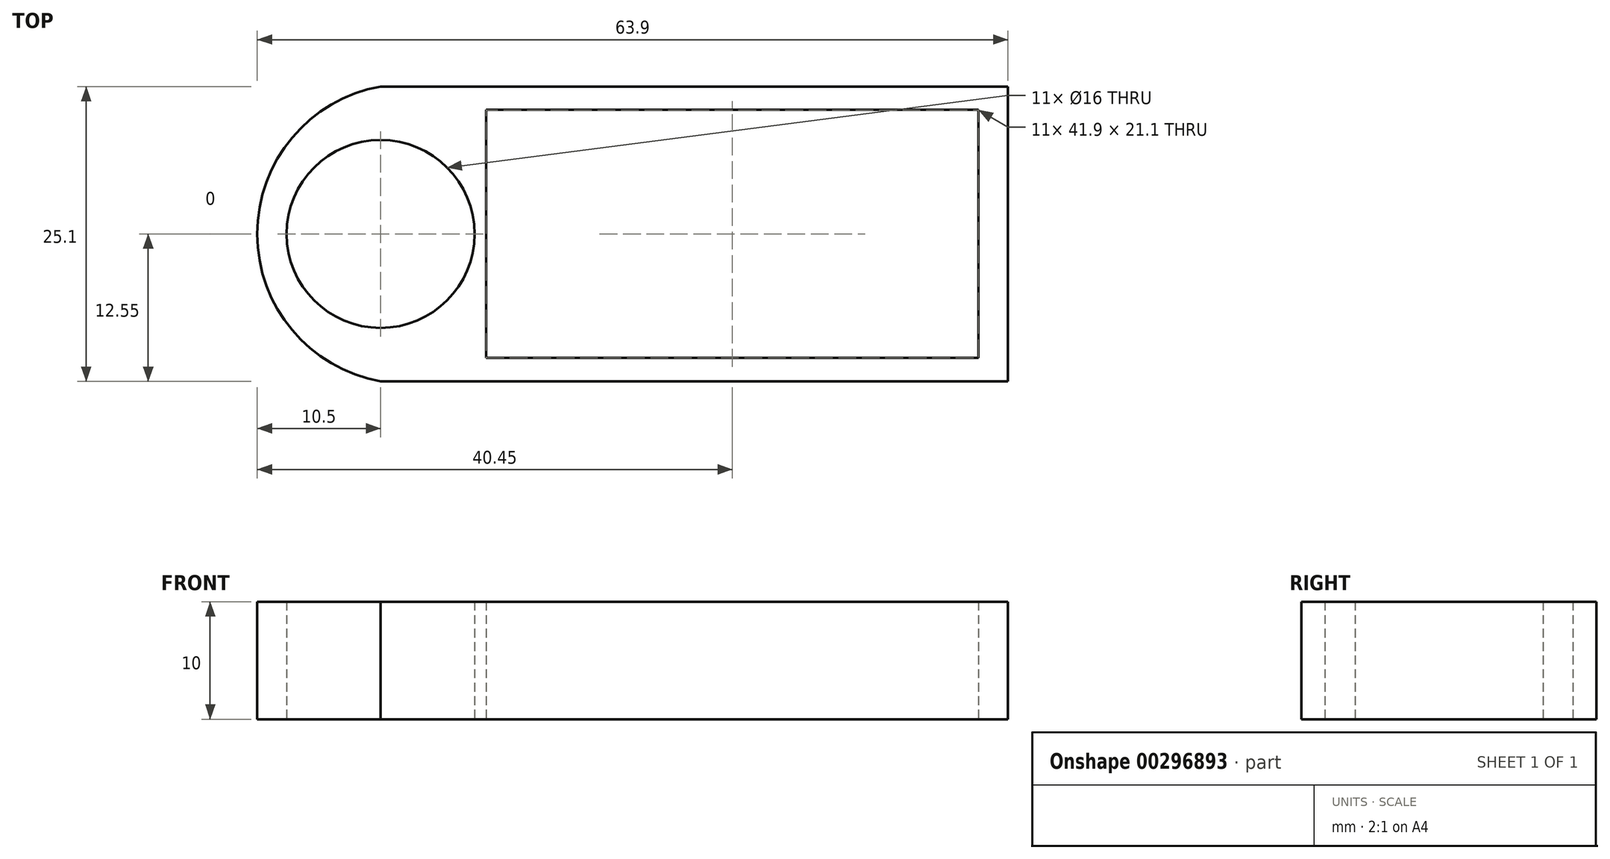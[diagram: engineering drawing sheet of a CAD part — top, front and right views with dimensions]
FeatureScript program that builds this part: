
annotation { "Feature Type Name" : "Feature", "Feature Type Description" : "" }
export const myFeature = defineFeature(function(context is Context, id is Id, definition is map)
    precondition{}
    {
        {
            var Q0;
            Q0=qCreatedBy(makeId("Top.planeOp"),FACE);
            var sketch = newSketch(context, id + "F0", { "sketchPlane" : qUnion([Q0])});
            skLineSegment(sketch, "E0.bottom", {"start": v(26.7, 12.55) * mm, "end": v(-26.7, 12.55) * mm});
            skLineSegment(sketch, "E0.top", {"start": v(26.7, -12.55) * mm, "end": v(-26.7, -12.55) * mm});
            skLineSegment(sketch, "E0.left", {"start": v(26.7, 12.55) * mm, "end": v(26.7, -12.55) * mm});
            skLineSegment(sketch, "E0.right", {"start": v(-26.7, 12.55) * mm, "end": v(-26.7, -12.55) * mm, "construction": true});
            skPoint(sketch, "E0.middle", {"position": v(0, 0) * mm});
            skLineSegment(sketch, "E1.bottom", {"start": v(-17.7, 10.55) * mm, "end": v(24.2, 10.55) * mm});
            skLineSegment(sketch, "E1.top", {"start": v(-17.7, -10.55) * mm, "end": v(24.2, -10.55) * mm});
            skLineSegment(sketch, "E1.left", {"start": v(-17.7, 10.55) * mm, "end": v(-17.7, -10.55) * mm});
            skLineSegment(sketch, "E1.right", {"start": v(24.2, 10.55) * mm, "end": v(24.2, -10.55) * mm});
            skLineSegment(sketch, "E2", {"start": v(-36.3, 0) * mm, "end": v(83.65, 0) * mm, "construction": true});
            skPoint(sketch, "E3", {"position": v(-26.7, 0) * mm});
            skCircle(sketch, "E4", {"center": v(-26.7, 0) * mm, "radius": 8 * mm});
            skArc(sketch, "E5", {"start": v(-26.7, 12.55) * mm, "mid": v(-37.2, 0) * mm, "end": v(-26.7, -12.55) * mm});
            skPoint(sketch, "E6", {"position": v(-37.2, 0) * mm});
            skPoint(sketch, "E7", {"position": v(-34.7, 0) * mm});
            skSolve(sketch);
        }
        {
            var Q0;
            Q0 = qSketchRegion(id + "F0", true);
            extrude(context, id + "F1", {"entities" : qUnion([Q0]), "depth" : 10 * mm});
        }
    });
